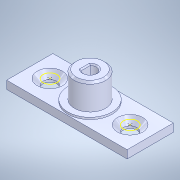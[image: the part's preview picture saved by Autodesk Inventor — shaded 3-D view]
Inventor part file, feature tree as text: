
AUTODESK INVENTOR PART (.ipt)
format: ipt  version: 2021 (Build 250183000, 183)  size: 175,616 bytes
history: native  units: in
note: dims shown in document units (in); Inventor stores cm internally (conversion verified against a paired STEP export)
features: sketch x5, extrude x3, other x3, chamfer x2, reference x2, hole x1, projected_geometry x1
ambient origin geometry x8: Origin, YZ Plane, XZ Plane, XY Plane, X Axis, Y Axis, Z Axis, Center Point
bodies: Solid1 (feature_tree)
feature tree (17):
  extrude  "Extrusion1"  Depth=0.3937in TaperAngle=0.0deg
  extrude  "Extrusion2"  Depth=0.3937in TaperAngle=0.0deg
  extrude  "Extrusion3"  Depth=0.002in
  chamfer  "Chamfer1"  Distance=0.0118in Angle=45.0deg
  sketch  "Sketch4"  dims[d19=0.1339in d20=0.2362in d21=0.248in d22=0.0787in d23=90.0deg d24=0.315in d25=0.0in d26=0.002in]
  hole  "Hole2"  [1 undecoded]
  chamfer  "Chamfer2"  [1 undecoded]
  sketch  "Sketch1"  dims[d1=0.3937in d2=0.0in d3=0.3937in d4=0.0in]
  projected_geometry  "Projected Loop1"
  sketch  "Sketch2"  dims[d5=0.0039in d6=0.3937in d7=0.0in]
  sketch  "Sketch3"  dims[d8=0.0197in d9=0.0787in d10=45.0deg]
  reference  "Reference1"
  reference  "Reference2"
  sketch  "Sketch6"  dims[d27=0.002in d28=0.0118in d29=0.0787in d30=45.0deg]
  other  "CSK for M4 Countersunk Flat Head Screw1"
  other  "sub_assy_robot_arm_link1.iam"
  other  "arm_1_v2:1"
note: 2 required parameter values undecoded (feature->parameter linkage not recoverable at this tier; creation-order binding heuristic only, values carry confidence <= 0.55)
